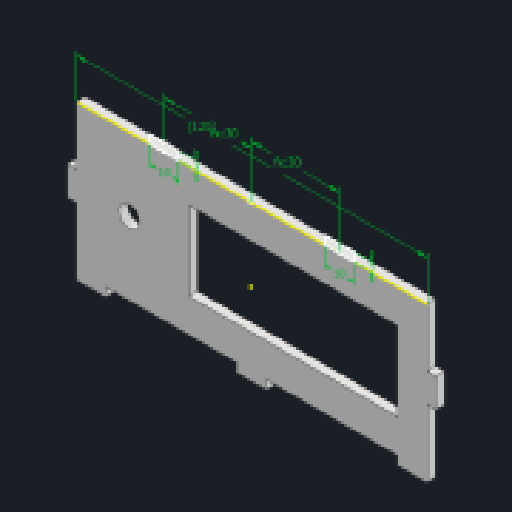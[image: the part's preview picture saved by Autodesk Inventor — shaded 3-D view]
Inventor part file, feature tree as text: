
AUTODESK INVENTOR PART (.ipt)
format: ipt  version: 2023 (Build 270158000, 158)  size: 187,904 bytes
history: native  units: mm
features: extrude x3, sketch x3
ambient origin geometry x8: Origin, YZ Plane, XZ Plane, XY Plane, X Axis, Y Axis, Z Axis, Center Point
bodies: Solid1 (feature_tree)
feature tree (6):
  extrude  "Extrusion1"  Depth=50.0mm
  extrude  "Extrusion2"  Depth=71.5mm
  extrude  "Extrusion3"  Depth=3.0mm
  sketch  "Sketch1"  dims[d0=120.0mm d1=50.0mm]
  sketch  "Sketch2"  dims[d2=27.0mm d3=71.5mm]
  sketch  "Sketch3"  dims[d4=10.0mm d6=18.7mm d7=26.2mm d8=7.0mm d9=8.4mm d10=12.0mm d11=10.0mm d12=3.0mm d13=10.0mm d14=3.0mm d15=10.0mm d16=3.0mm d17=10.0mm d18=3.0mm d19=10.0mm d20=3.0mm d21=10.0mm d22=3.0mm d23=3.0mm d24=10.0mm d25=3.0mm d26=10.0mm d27=3.0mm d28=0.0mm d29=0.0mm d30=0.0mm d31=120.0mm d32=10.0mm d33=3.0mm d34=10.0mm d35=3.0mm d36=30.0mm d37=30.0mm d38=3.0mm d39=0.0mm]
